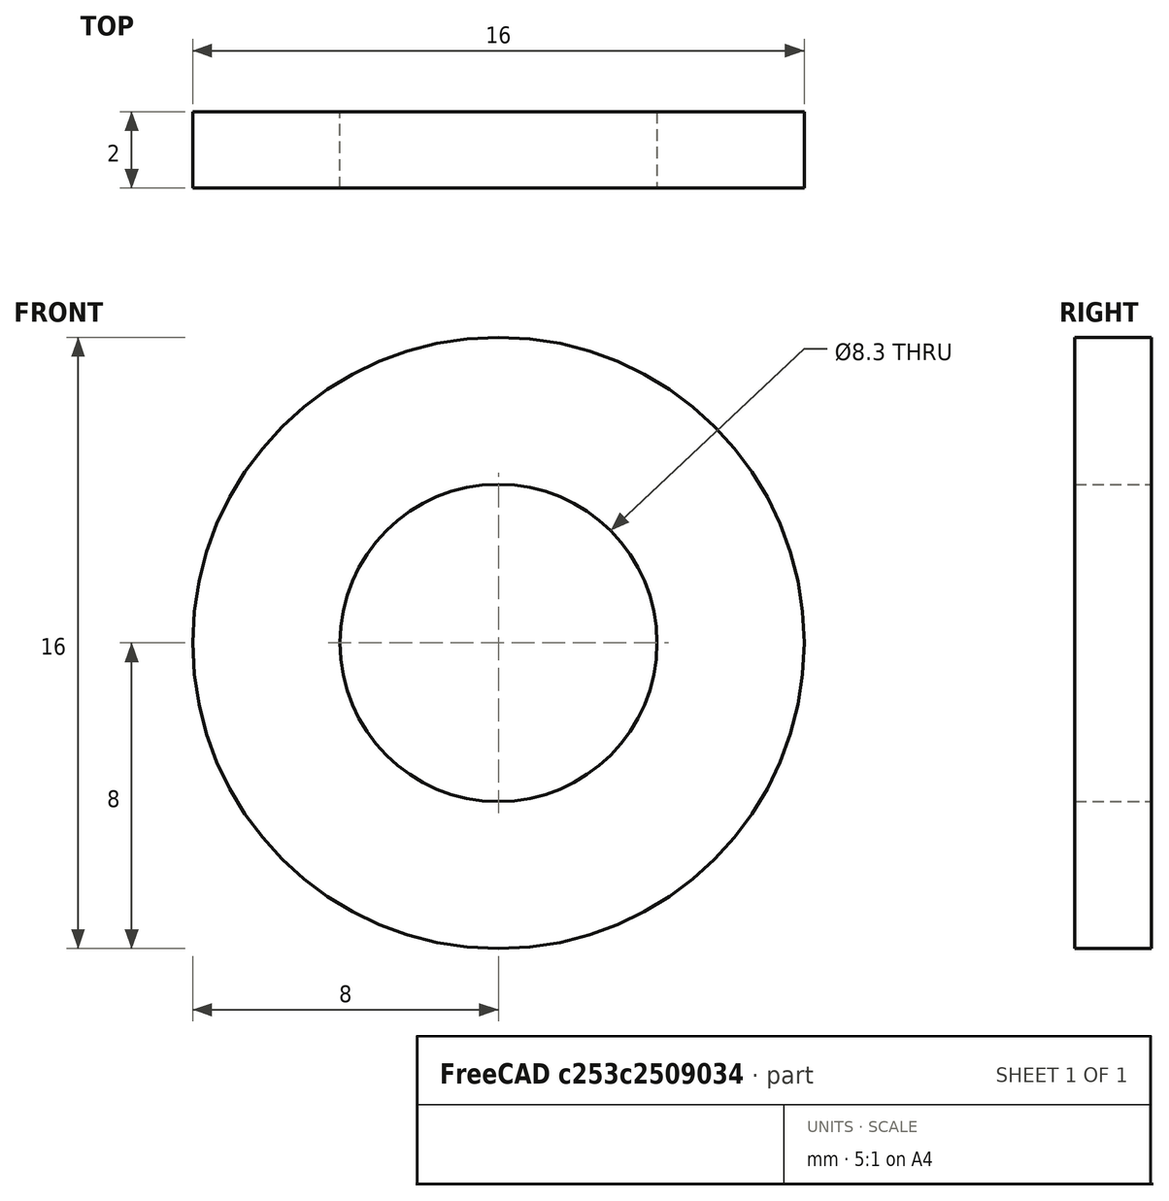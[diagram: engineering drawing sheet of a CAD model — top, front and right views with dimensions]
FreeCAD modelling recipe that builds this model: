
FCSTD DOCUMENT  (FreeCAD 0.19R17089 +1543 (Git))
Label: asm
License: All rights reserved
LicenseURL: http://en.wikipedia.org/wiki/All_rights_reserved
objects: Part::FeaturePython×4, App::FeaturePython×2, Sketcher::SketchObject×1, PartDesign::Pad×1, PartDesign::Body×1
note: 7 computed .brp shape members not serialized (recipe doc carries the construction recipe); baked Part::Feature solids carry a one-line shape summary decoded from their .brp

FEATURE [Sketcher::SketchObject] Sketch
  MapMode = 5
  Placement = pos=(0,0,0) rot=(1,0,0;1.5708rad)
  Support = -> [XZ_Plane]
  sketch-geometry (2):
    g0: Circle CenterX=0 CenterY=0 CenterZ=0 NormalX=0 NormalY=0 NormalZ=1 AngleXU=0 Radius=4.15
    g1: Circle CenterX=0 CenterY=0 CenterZ=0 NormalX=0 NormalY=0 NormalZ=1 AngleXU=0 Radius=8
  constraints (4):
    c: Coincident(g0,g-1)
    c: Coincident(g1,g0)
    c: Diameter(g0) = 8.3  'D1'
    c: Diameter(g1) = 16  'D2'
FEATURE [PartDesign::Pad] Pad
  ClaimChildren = false
  Length = 2
  Length2 = 100
  Placement = pos=(0,0,0) rot=(1,0,0;1.5708rad)
  Profile = -> Sketch
  Type = 0
FEATURE [PartDesign::Body] Body
  Group = -> [Sketch,Pad]
  Origin = -> Origin
  Tip = -> Pad
FEATURE [App::FeaturePython] Constraints  # WARN: FeaturePython — macro-defined, semantics opaque (R4)
  GroupMode = 1
  _Version = 1
FEATURE [Part::FeaturePython] Parts  # WARN: FeaturePython — macro-defined, semantics opaque (R4)
  Group = -> [Body]
  GroupMode = 0
FEATURE [Part::FeaturePython] Assembly  label="Assembly000 000"  # WARN: FeaturePython — macro-defined, semantics opaque (R4)
  AutoRelax = true
  BuildShape = 0
  Freeze = false
  Group = -> [Constraints,Elements,Parts]
  GroupMode = 1
  SolverType = 1
  Verbose = false
  _SolverType = 1
  _Version = 1
FEATURE [App::FeaturePython] Elements  # WARN: FeaturePython — macro-defined, semantics opaque (R4)
  Group = -> [Element,Element001]
  GroupMode = 1
FEATURE [Part::FeaturePython] Element  # link proxy (typed FeaturePython)
  Detach = false
  LinkTransform = true
  LinkedObject = -> Body [Pad.Edge5]
  _Parent = -> Elements
FEATURE [Part::FeaturePython] Element001  # link proxy (typed FeaturePython)
  Detach = false
  LinkTransform = true
  LinkedObject = -> Body [Pad.Edge6]
  _Parent = -> Elements
